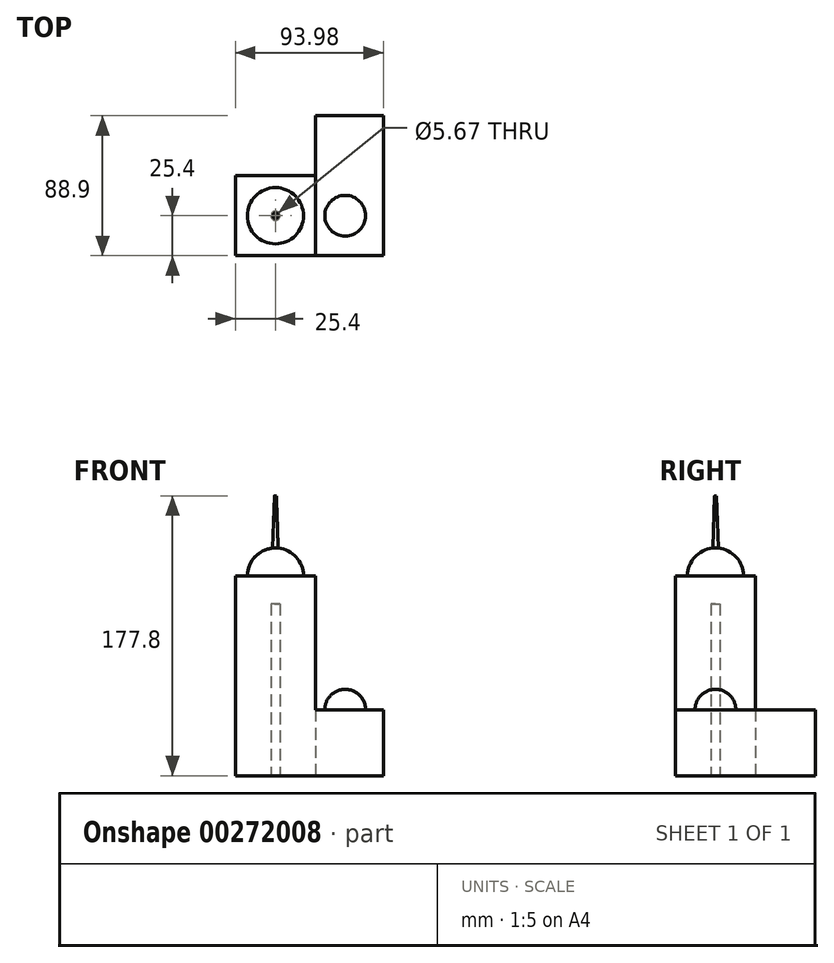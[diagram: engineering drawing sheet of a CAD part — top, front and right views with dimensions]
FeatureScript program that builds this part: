
annotation { "Feature Type Name" : "Feature", "Feature Type Description" : "" }
export const myFeature = defineFeature(function(context is Context, id is Id, definition is map)
    precondition{}
    {
        {
            var Q0;
            Q0=qCreatedBy(makeId("Top.planeOp"),FACE);
            var sketch = newSketch(context, id + "F0", { "sketchPlane" : qUnion([Q0])});
            skLineSegment(sketch, "E0.bottom", {"start": v(25.4, -25.4) * mm, "end": v(-25.4, -25.4) * mm});
            skLineSegment(sketch, "E0.top", {"start": v(25.4, 25.4) * mm, "end": v(-25.4, 25.4) * mm});
            skLineSegment(sketch, "E0.left", {"start": v(25.4, -25.4) * mm, "end": v(25.4, 25.4) * mm});
            skLineSegment(sketch, "E0.right", {"start": v(-25.4, -25.4) * mm, "end": v(-25.4, 25.4) * mm});
            skPoint(sketch, "E0.middle", {"position": v(0, 0) * mm});
            skCircle(sketch, "E1", {"center": v(0, 0) * mm, "radius": 2.83 * mm});
            skLineSegment(sketch, "E2.bottom", {"start": v(25.4, 25.4) * mm, "end": v(68.58, 25.4) * mm});
            skLineSegment(sketch, "E2.top", {"start": v(25.4, -25.4) * mm, "end": v(68.58, -25.4) * mm});
            skLineSegment(sketch, "E2.left", {"start": v(25.4, 25.4) * mm, "end": v(25.4, -25.4) * mm});
            skLineSegment(sketch, "E2.right", {"start": v(68.58, 25.4) * mm, "end": v(68.58, -25.4) * mm});
            skLineSegment(sketch, "E3.top", {"start": v(25.4, 63.5) * mm, "end": v(68.58, 63.5) * mm});
            skLineSegment(sketch, "E3.left", {"start": v(25.4, 25.4) * mm, "end": v(25.4, 63.5) * mm});
            skLineSegment(sketch, "E3.right", {"start": v(68.58, 25.4) * mm, "end": v(68.58, 63.5) * mm});
            skSolve(sketch);
        }
        {
            var Q0;
            Q0=makeQuery(id+"F0.imprint","IMPRINT",FACE,{"disambiguationData":[TD([[makeQuery(id+"F0.imprint","IMPRINT",EDGE,{"derivedFrom":sQuery(id+"F0.wireOp",EDGE,"E0.bottom")}),-1.0]])]});
            extrude(context, id + "F1", {"entities" : qUnion([Q0]), "depth" : 127 * mm});
        }
        {
            var Q0;
            Q0=qCreatedBy(makeId("Front.planeOp"),FACE);
            var sketch = newSketch(context, id + "F2", { "sketchPlane" : qUnion([Q0])});
            skLineSegment(sketch, "E4", {"start": v(0, 152.98) * mm, "end": v(0, -3.66) * mm});
            skArc(sketch, "E5", {"start": v(0, 144.63) * mm, "mid": v(-17.84, 126.8) * mm, "end": v(0, 108.96) * mm});
            skSolve(sketch);
        }
        {
            var Q0;
            {var subQ0=sQuery(id+"F2.wireOp",EDGE,"E5");Q0=makeQuery(id+"F2.imprint","IMPRINT",FACE,{"disambiguationData":[TD([[makeQuery(id+"F2.imprint","IMPRINT",EDGE,{"derivedFrom":subQ0}),1.0]])]});}
            var Q1;
            Q1=sQuery(id+"F2.wireOp",EDGE,"E4");
            revolve(context, id + "F3", {"operationType" : NewBodyOperationType.ADD, "entities" : qUnion([Q0]), "axis" : qUnion([Q1]), "revolveType" : RevolveType.FULL});
        }
        {
            var Q0;
            Q0=makeQuery(id+"F1.opExtrude","CAP_FACE",FACE,{"disambiguationData":[OSD([sQuery(id+"F0.wireOp",EDGE,"E0.bottom"),sQuery(id+"F0.wireOp",EDGE,"E0.top"),sQuery(id+"F0.wireOp",EDGE,"E0.left"),sQuery(id+"F0.wireOp",EDGE,"E0.right"),sQuery(id+"F0.wireOp",EDGE,"E1")])],"isStart":false});
            var sketch = newSketch(context, id + "F4", { "sketchPlane" : qUnion([Q0])});
            skCircle(sketch, "E6", {"center": v(0, 0) * mm, "radius": 2.36 * mm});
            skSolve(sketch);
        }
        {
            var Q0;
            Q0 = qSketchRegion(id + "F4", true);
            extrude(context, id + "F5", {"entities" : qUnion([Q0]), "operationType" : NewBodyOperationType.ADD, "depth" : 50.8 * mm, "hasDraft" : true, "draftAngle" : 2 * degree, "draftPullDirection" : true});
        }
        {
            var Q0;
            Q0 = qSketchRegion(id + "F0", true);
            extrude(context, id + "F6", {"entities" : qUnion([Q0]), "operationType" : NewBodyOperationType.ADD, "depth" : 41.9 * mm});
        }
        {
            var Q0;
            Q0=qCreatedBy(makeId("Front.planeOp"),FACE);
            var sketch = newSketch(context, id + "F7", { "sketchPlane" : qUnion([Q0])});
            skLineSegment(sketch, "E7", {"start": v(44.33, 67.9) * mm, "end": v(44.33, -6.96) * mm});
            skArc(sketch, "E8", {"start": v(44.33, 54.92) * mm, "mid": v(31.38, 41.96) * mm, "end": v(44.33, 29) * mm});
            skSolve(sketch);
        }
        {
            var Q0;
            Q0 = qSketchRegion(id + "F7", true);
            var Q1;
            Q1=sQuery(id+"F7.wireOp",EDGE,"E7");
            revolve(context, id + "F8", {"operationType" : NewBodyOperationType.ADD, "entities" : qUnion([Q0]), "axis" : qUnion([Q1]), "revolveType" : RevolveType.FULL});
        }
    });
